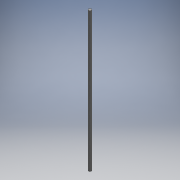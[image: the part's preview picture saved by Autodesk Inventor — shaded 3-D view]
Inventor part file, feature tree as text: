
AUTODESK INVENTOR PART (.ipt)
format: ipt  version: 2018 (Build 220112000, 112)  size: 92,160 bytes
history: native  units: mm
features: extrude x1, thread x1, sketch x1
ambient origin geometry x8: Origin, YZ Plane, XZ Plane, XY Plane, X Axis, Y Axis, Z Axis, Center Point
bodies: Solid1 (feature_tree)
feature tree (3):
  extrude  "Extrusion1"  Depth=300.0mm TaperAngle=0.0deg
  thread  "Thread1"  [1 undecoded]
  sketch  "Sketch1"  dims[d0=6.0mm d1=300.0mm d2=0.0mm d3=10.0mm d4=0.0mm]
note: 1 required parameter value undecoded (feature->parameter linkage not recoverable at this tier; creation-order binding heuristic only, values carry confidence <= 0.55)
